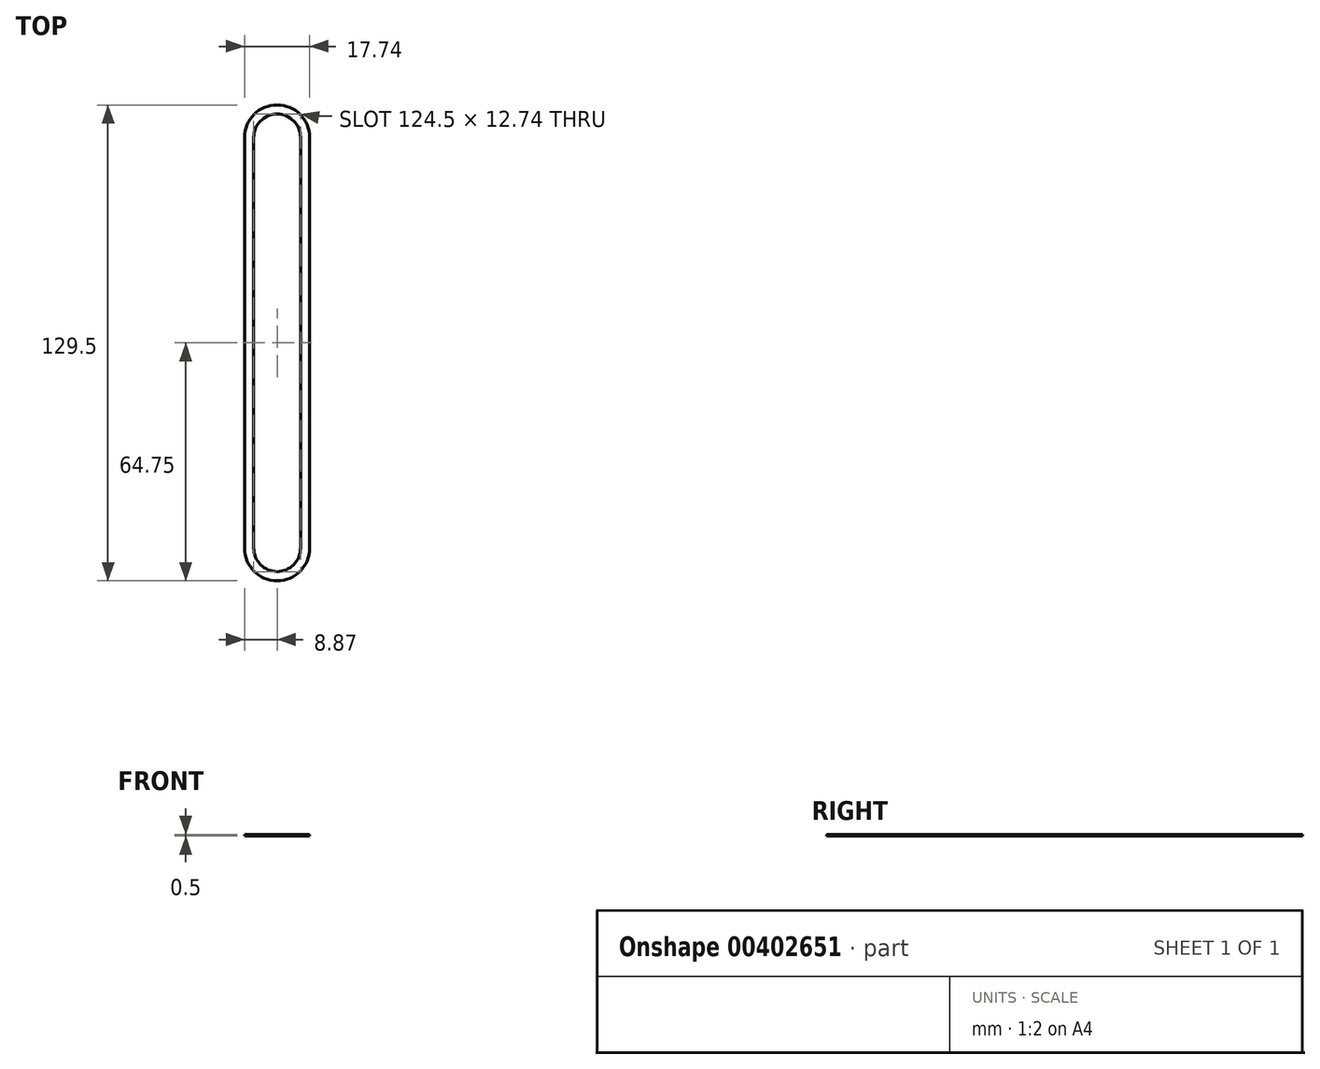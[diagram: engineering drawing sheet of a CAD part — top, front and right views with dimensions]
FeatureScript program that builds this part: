
annotation { "Feature Type Name" : "Feature", "Feature Type Description" : "" }
export const myFeature = defineFeature(function(context is Context, id is Id, definition is map)
    precondition{}
    {
        {
            var Q0;
            Q0=qCreatedBy(makeId("Front.planeOp"),FACE);
            var sketch = newSketch(context, id + "F0", { "sketchPlane" : qUnion([Q0])});
            skLineSegment(sketch, "E0.bottom", {"start": v(1.25, 0.25) * mm, "end": v(-1.25, 0.25) * mm});
            skLineSegment(sketch, "E0.top", {"start": v(1.25, -0.25) * mm, "end": v(-1.25, -0.25) * mm});
            skLineSegment(sketch, "E0.left", {"start": v(1.25, 0.25) * mm, "end": v(1.25, -0.25) * mm});
            skLineSegment(sketch, "E0.right", {"start": v(-1.25, 0.25) * mm, "end": v(-1.25, -0.25) * mm});
            skPoint(sketch, "E0.middle", {"position": v(0, 0) * mm});
            skSolve(sketch);
        }
        {
            var Q0;
            Q0=qCreatedBy(makeId("Top.planeOp"),FACE);
            var sketch = newSketch(context, id + "F1", { "sketchPlane" : qUnion([Q0])});
            skLineSegment(sketch, "E1", {"start": v(0, 0) * mm, "end": v(0, 55.88) * mm});
            skLineSegment(sketch, "E2", {"start": v(0, 0) * mm, "end": v(0, -55.88) * mm});
            skArc(sketch, "E3", {"start": v(-15.24, -55.88) * mm, "mid": v(-7.62, -63.5) * mm, "end": v(0, -55.88) * mm});
            skArc(sketch, "E4", {"start": v(0, 55.88) * mm, "mid": v(-7.62, 63.5) * mm, "end": v(-15.24, 55.88) * mm});
            skLineSegment(sketch, "E5", {"start": v(-15.24, 55.88) * mm, "end": v(-15.24, -55.88) * mm});
            skSolve(sketch);
        }
        {
            var Q0;
            Q0=makeQuery(id+"F0.imprint","IMPRINT",FACE,{"disambiguationData":[TD([[makeQuery(id+"F0.imprint","IMPRINT",EDGE,{"derivedFrom":sQuery(id+"F0.wireOp",EDGE,"E0.bottom")}),1.0]])]});
            var Q1;
            Q1=sQuery(id+"F1.wireOp",EDGE,"E1");
            var Q2;
            Q2=sQuery(id+"F1.wireOp",EDGE,"E4");
            var Q3;
            Q3=sQuery(id+"F1.wireOp",EDGE,"E5");
            var Q4;
            Q4=sQuery(id+"F1.wireOp",EDGE,"E2");
            var Q5;
            Q5=sQuery(id+"F1.wireOp",EDGE,"E3");
            sweep(context, id + "F2", {"profiles" : qUnion([Q0]), "path" : qUnion([Q1, Q2, Q3, Q4, Q5])});
        }
    });
